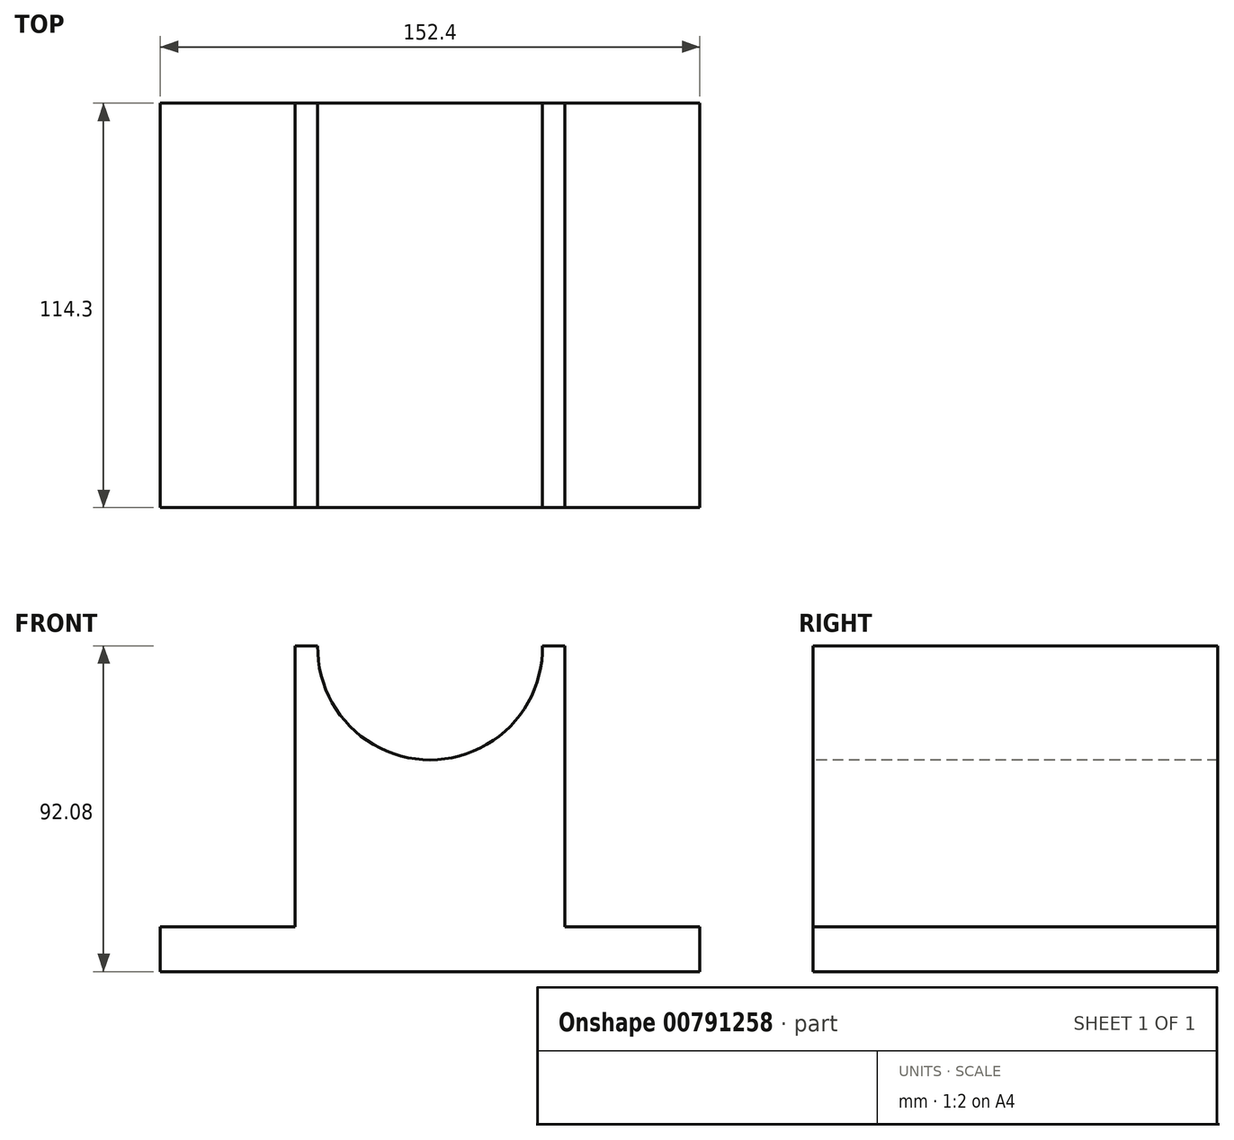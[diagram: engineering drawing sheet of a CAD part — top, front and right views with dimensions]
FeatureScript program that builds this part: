
annotation { "Feature Type Name" : "Feature", "Feature Type Description" : "" }
export const myFeature = defineFeature(function(context is Context, id is Id, definition is map)
    precondition{}
    {
        {
            var Q0;
            Q0=qCreatedBy(makeId("Front.planeOp"),FACE);
            var sketch = newSketch(context, id + "F0", { "sketchPlane" : qUnion([Q0])});
            skLineSegment(sketch, "E0", {"start": v(-76.1, 0) * mm, "end": v(76.3, 0) * mm});
            skLineSegment(sketch, "E1", {"start": v(76.3, 0) * mm, "end": v(76.3, 12.7) * mm});
            skLineSegment(sketch, "E2", {"start": v(76.3, 12.7) * mm, "end": v(38.2, 12.7) * mm});
            skLineSegment(sketch, "E3", {"start": v(38.2, 12.7) * mm, "end": v(38.2, 92.08) * mm});
            skLineSegment(sketch, "E4", {"start": v(38.2, 92.07) * mm, "end": v(-38, 92.07) * mm});
            skLineSegment(sketch, "E5", {"start": v(-38, 92.07) * mm, "end": v(-38, 12.7) * mm});
            skLineSegment(sketch, "E6", {"start": v(-38, 12.7) * mm, "end": v(-76.1, 12.7) * mm});
            skLineSegment(sketch, "E7", {"start": v(-76.1, 12.7) * mm, "end": v(-76.1, 0) * mm});
            skSolve(sketch);
        }
        {
            var Q0;
            Q0 = qSketchRegion(id + "F0", true);
            extrude(context, id + "F1", {"entities" : qUnion([Q0]), "depth" : 114.3 * mm, "offsetDistance" : 25.4 * mm});
        }
        {
            var Q0;
            Q0=makeQuery(id+"F1.opExtrude","CAP_FACE",FACE,{"disambiguationData":[OSD([sQuery(id+"F0.wireOp",EDGE,"E0"),sQuery(id+"F0.wireOp",EDGE,"E1"),sQuery(id+"F0.wireOp",EDGE,"E2"),sQuery(id+"F0.wireOp",EDGE,"E3"),sQuery(id+"F0.wireOp",EDGE,"E4"),sQuery(id+"F0.wireOp",EDGE,"E5"),sQuery(id+"F0.wireOp",EDGE,"E6"),sQuery(id+"F0.wireOp",EDGE,"E7")])],"isStart":false});
            var sketch = newSketch(context, id + "F2", { "sketchPlane" : qUnion([Q0])});
            skLineSegment(sketch, "E8", {"start": v(-38, 92.07) * mm, "end": v(-31.65, 92.07) * mm});
            skLineSegment(sketch, "E9", {"start": v(38.2, 92.07) * mm, "end": v(31.85, 92.07) * mm});
            skArc(sketch, "E10", {"start": v(-31.65, 92.07) * mm, "mid": v(0.1, 59.93) * mm, "end": v(31.85, 92.07) * mm, "construction": true});
            skArc(sketch, "E11", {"start": v(-31.65, 92.07) * mm, "mid": v(0.1, 59.82) * mm, "end": v(31.85, 92.07) * mm});
            skSolve(sketch);
        }
        {
            var Q0;
            Q0 = qSketchRegion(id + "F2", true);
            var Q1;
            {var subQ0=sQuery(id+"F2.wireOp",EDGE,"E11");Q1=makeQuery(id+"F2.imprint","IMPRINT",FACE,{"disambiguationData":[TD([[makeQuery(id+"F2.imprint","IMPRINT",EDGE,{"derivedFrom":subQ0}),1.0]])]});}
            extrude(context, id + "F3", {"entities" : qUnion([Q0, Q1]), "operationType" : NewBodyOperationType.REMOVE, "endBound" : BoundingType.UP_TO_NEXT, "oppositeDirection" : true, "depth" : 25.4 * mm, "offsetDistance" : 25.4 * mm});
        }
    });
